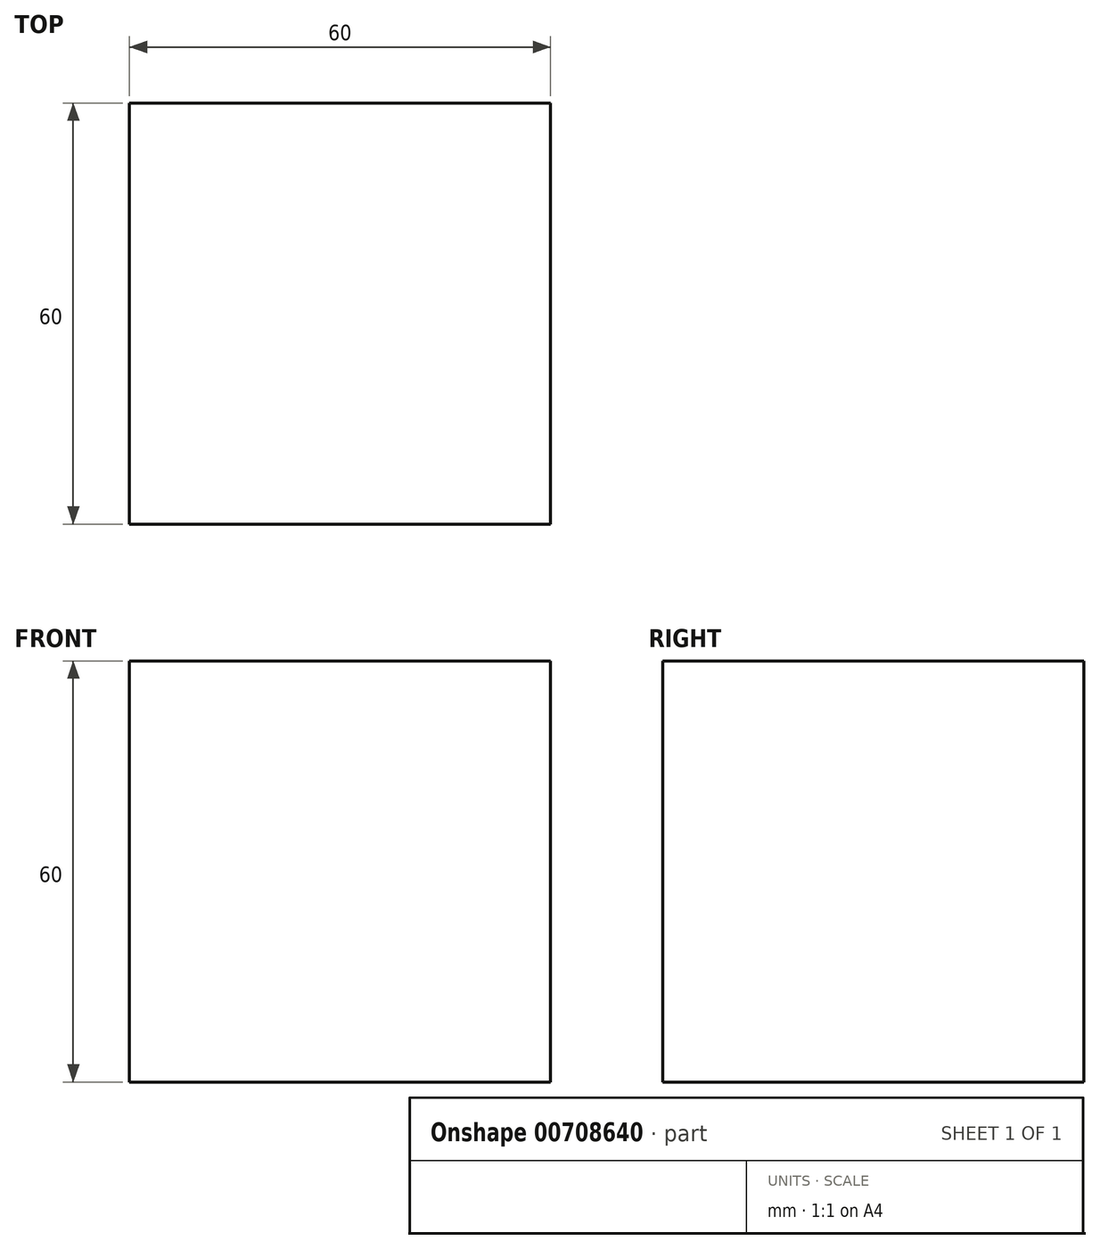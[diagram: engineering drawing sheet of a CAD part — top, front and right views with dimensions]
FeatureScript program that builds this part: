
annotation { "Feature Type Name" : "Feature", "Feature Type Description" : "" }
export const myFeature = defineFeature(function(context is Context, id is Id, definition is map)
    precondition{}
    {
        {
            var Q0;
            Q0=qCreatedBy(makeId("Top.planeOp"),FACE);
            var sketch = newSketch(context, id + "F0", { "sketchPlane" : qUnion([Q0])});
            skLineSegment(sketch, "E0.bottom", {"start": v(30, 30) * mm, "end": v(-30, 30) * mm});
            skLineSegment(sketch, "E0.top", {"start": v(30, -30) * mm, "end": v(-30, -30) * mm});
            skLineSegment(sketch, "E0.left", {"start": v(30, 30) * mm, "end": v(30, -30) * mm});
            skLineSegment(sketch, "E0.right", {"start": v(-30, 30) * mm, "end": v(-30, -30) * mm});
            skPoint(sketch, "E0.middle", {"position": v(0, 0) * mm});
            skSolve(sketch);
        }
        {
            var Q0;
            Q0 = qSketchRegion(id + "F0", true);
            extrude(context, id + "F1", {"entities" : qUnion([Q0]), "depth" : 60 * mm, "offsetDistance" : 25 * mm});
        }
    });
